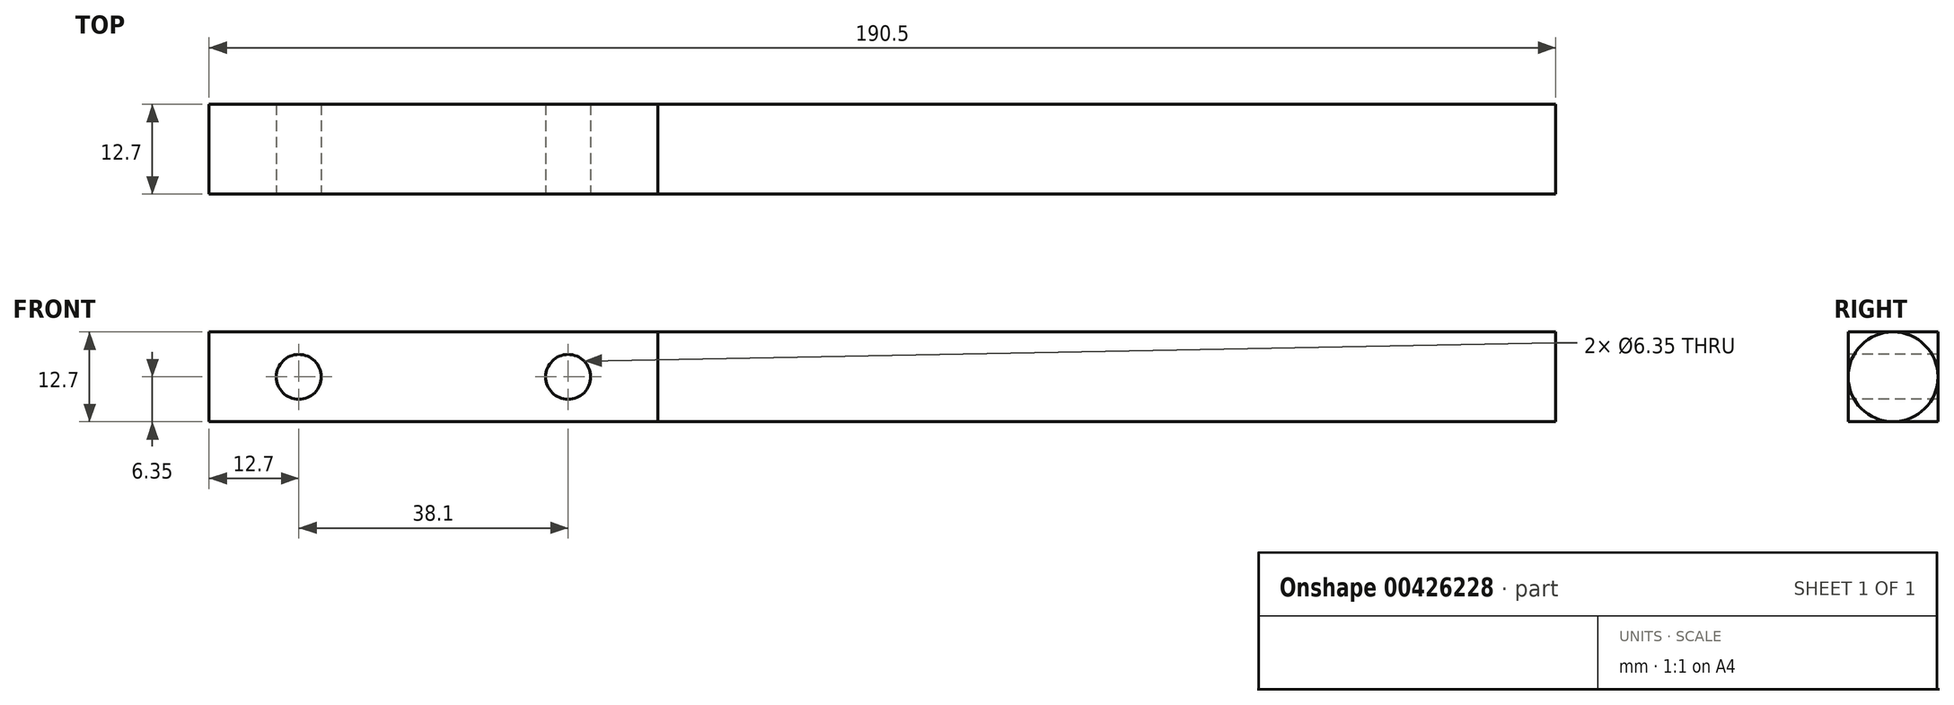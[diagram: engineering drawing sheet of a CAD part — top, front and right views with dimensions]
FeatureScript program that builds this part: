
annotation { "Feature Type Name" : "Feature", "Feature Type Description" : "" }
export const myFeature = defineFeature(function(context is Context, id is Id, definition is map)
    precondition{}
    {
        {
            var Q0;
            Q0=qCreatedBy(makeId("Front.planeOp"),FACE);
            var sketch = newSketch(context, id + "F0", { "sketchPlane" : qUnion([Q0])});
            skLineSegment(sketch, "E0.bottom", {"start": v(0, -6.35) * mm, "end": v(-63.5, -6.35) * mm});
            skLineSegment(sketch, "E0.top", {"start": v(0, 6.35) * mm, "end": v(-63.5, 6.35) * mm});
            skLineSegment(sketch, "E0.left", {"start": v(0, -6.35) * mm, "end": v(0, 6.35) * mm});
            skLineSegment(sketch, "E0.right", {"start": v(-63.5, -6.35) * mm, "end": v(-63.5, 6.35) * mm});
            skSolve(sketch);
        }
        {
            var Q0;
            Q0 = qSketchRegion(id + "F0", true);
            extrude(context, id + "F1", {"entities" : qUnion([Q0]), "endBound" : BoundingType.SYMMETRIC, "depth" : 12.7 * mm});
        }
        {
            var Q0;
            Q0=qCreatedBy(makeId("Front.planeOp"),FACE);
            var sketch = newSketch(context, id + "F2", { "sketchPlane" : qUnion([Q0])});
            skLineSegment(sketch, "E1.bottom", {"start": v(0, 0) * mm, "end": v(127, 0) * mm});
            skLineSegment(sketch, "E1.top", {"start": v(0, 6.35) * mm, "end": v(127, 6.35) * mm});
            skLineSegment(sketch, "E1.left", {"start": v(0, 0) * mm, "end": v(0, 6.35) * mm});
            skLineSegment(sketch, "E1.right", {"start": v(127, 0) * mm, "end": v(127, 6.35) * mm});
            skSolve(sketch);
        }
        {
            var Q0;
            Q0=makeQuery(id+"F2.imprint","IMPRINT",FACE,{"disambiguationData":[TD([[makeQuery(id+"F2.imprint","IMPRINT",EDGE,{"derivedFrom":sQuery(id+"F2.wireOp",EDGE,"E1.bottom")}),1.0]])]});
            var Q1;
            Q1=sQuery(id+"F2.wireOp",EDGE,"E1.bottom");
            revolve(context, id + "F3", {"operationType" : NewBodyOperationType.ADD, "entities" : qUnion([Q0]), "axis" : qUnion([Q1]), "revolveType" : RevolveType.FULL});
        }
        {
            var Q0;
            Q0=makeQuery(id+"F1.opExtrude","CAP_FACE",FACE,{"disambiguationData":[OSD([sQuery(id+"F0.wireOp",EDGE,"E0.bottom"),sQuery(id+"F0.wireOp",EDGE,"E0.top"),sQuery(id+"F0.wireOp",EDGE,"E0.left"),sQuery(id+"F0.wireOp",EDGE,"E0.right")])],"isStart":false});
            var sketch = newSketch(context, id + "F4", { "sketchPlane" : qUnion([Q0])});
            skCircle(sketch, "E2", {"center": v(-50.8, 0) * mm, "radius": 3.18 * mm});
            skCircle(sketch, "E3", {"center": v(-12.7, 0) * mm, "radius": 3.18 * mm});
            skSolve(sketch);
        }
        {
            var Q0;
            Q0 = qSketchRegion(id + "F4", true);
            extrude(context, id + "F5", {"entities" : qUnion([Q0]), "operationType" : NewBodyOperationType.REMOVE, "endBound" : BoundingType.THROUGH_ALL, "oppositeDirection" : true, "depth" : 25.4 * mm});
        }
    });
